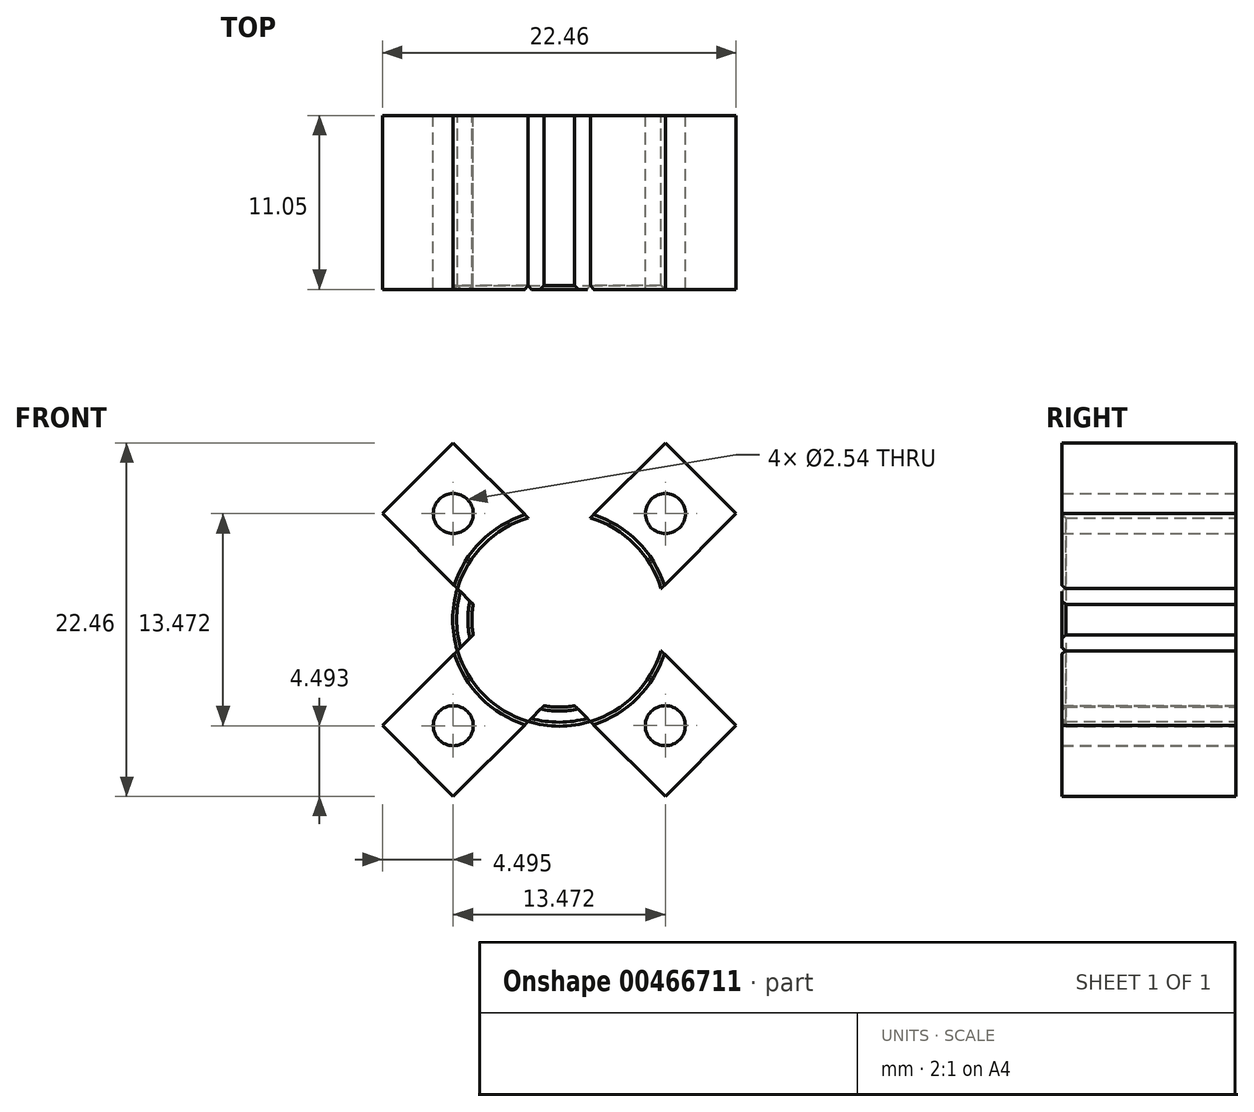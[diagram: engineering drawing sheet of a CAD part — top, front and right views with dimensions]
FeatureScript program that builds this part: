
annotation { "Feature Type Name" : "Feature", "Feature Type Description" : "" }
export const myFeature = defineFeature(function(context is Context, id is Id, definition is map)
    precondition{}
    {
        {
            var Q0;
            Q0=qCreatedBy(makeId("Front.planeOp"),FACE);
            var sketch = newSketch(context, id + "F0", { "sketchPlane" : qUnion([Q0])});
            skLineSegment(sketch, "E0.bottom", {"start": v(11.23, -6.74) * mm, "end": v(-6.74, 11.23) * mm});
            skLineSegment(sketch, "E0.top", {"start": v(6.74, -11.23) * mm, "end": v(-11.23, 6.74) * mm});
            skLineSegment(sketch, "E0.left", {"start": v(11.23, -6.74) * mm, "end": v(6.74, -11.23) * mm});
            skLineSegment(sketch, "E0.right", {"start": v(-6.74, 11.23) * mm, "end": v(-11.23, 6.74) * mm});
            skPoint(sketch, "E0.middle", {"position": v(0, 0) * mm});
            skLineSegment(sketch, "E1.bottom", {"start": v(11.23, 6.73) * mm, "end": v(6.73, 11.23) * mm});
            skLineSegment(sketch, "E1.top", {"start": v(-6.73, -11.23) * mm, "end": v(-11.23, -6.73) * mm});
            skLineSegment(sketch, "E1.left", {"start": v(11.23, 6.73) * mm, "end": v(-6.73, -11.23) * mm});
            skLineSegment(sketch, "E1.right", {"start": v(6.73, 11.23) * mm, "end": v(-11.23, -6.73) * mm});
            skCircle(sketch, "E2", {"center": v(6.74, -6.74) * mm, "radius": 1.27 * mm});
            skCircle(sketch, "E3", {"center": v(-6.73, -6.74) * mm, "radius": 1.27 * mm});
            skCircle(sketch, "E4", {"center": v(-6.74, 6.74) * mm, "radius": 1.27 * mm});
            skCircle(sketch, "E5", {"center": v(6.74, 6.73) * mm, "radius": 1.27 * mm});
            skCircle(sketch, "E6", {"center": v(0, 0) * mm, "radius": 5.56 * mm});
            skCircle(sketch, "E7.0", {"center": v(0, 0) * mm, "radius": 6.77 * mm});
            skSolve(sketch);
        }
        {
            var Q0;
            {var subQ1=sQuery(id+"F0.wireOp",EDGE,"E1.top");Q0=makeQuery(id+"F0.imprint","IMPRINT",FACE,{"disambiguationData":[TD([[makeQuery(id+"F0.imprint","IMPRINT",EDGE,{"derivedFrom":subQ1}),-1.0]])]});}
            var Q1;
            {var subQ0=sQuery(id+"F0.wireOp",EDGE,"E0.left");Q1=makeQuery(id+"F0.imprint","IMPRINT",FACE,{"disambiguationData":[TD([[makeQuery(id+"F0.imprint","IMPRINT",EDGE,{"derivedFrom":subQ0}),-1.0]])]});}
            var Q2;
            {var subQ0=sQuery(id+"F0.wireOp",EDGE,"E0.right");Q2=makeQuery(id+"F0.imprint","IMPRINT",FACE,{"disambiguationData":[TD([[makeQuery(id+"F0.imprint","IMPRINT",EDGE,{"derivedFrom":subQ0}),1.0]])]});}
            var Q3;
            {var subQ1=sQuery(id+"F0.wireOp",EDGE,"E1.bottom");Q3=makeQuery(id+"F0.imprint","IMPRINT",FACE,{"disambiguationData":[TD([[makeQuery(id+"F0.imprint","IMPRINT",EDGE,{"derivedFrom":subQ1}),1.0]])]});}
            var Q4;
            {var subQ0=sQuery(id+"F0.wireOp",EDGE,"E7.0");var subQ1=sQuery(id+"F0.wireOp",EDGE,"E0.top");var subQ2=makeQuery(id+"F0.imprint","INTERSECT",VERTEX,{"disambiguationData":[OD(0.0)],"derivedFrom":[subQ1,subQ0]});Q4=makeQuery(id+"F0.imprint","IMPRINT",FACE,{"disambiguationData":[TD([[makeQuery(id+"F0.imprint","IMPRINT",EDGE,{"disambiguationData":[TD([[subQ2,-1.0]])],"derivedFrom":subQ1}),1.0]])]});}
            var Q5;
            {var subQ0=sQuery(id+"F0.wireOp",EDGE,"E7.0");var subQ1=sQuery(id+"F0.wireOp",EDGE,"E0.bottom");var subQ2=makeQuery(id+"F0.imprint","INTERSECT",VERTEX,{"disambiguationData":[OD(0.0)],"derivedFrom":[subQ1,subQ0]});Q5=makeQuery(id+"F0.imprint","IMPRINT",FACE,{"disambiguationData":[TD([[makeQuery(id+"F0.imprint","IMPRINT",EDGE,{"disambiguationData":[TD([[subQ2,-1.0]])],"derivedFrom":subQ1}),1.0]])]});}
            var Q6;
            {var subQ0=sQuery(id+"F0.wireOp",EDGE,"E7.0");var subQ1=sQuery(id+"F0.wireOp",EDGE,"E1.left");var subQ2=makeQuery(id+"F0.imprint","INTERSECT",VERTEX,{"disambiguationData":[OD(1.0)],"derivedFrom":[subQ1,subQ0]});Q6=makeQuery(id+"F0.imprint","IMPRINT",FACE,{"disambiguationData":[TD([[makeQuery(id+"F0.imprint","IMPRINT",EDGE,{"disambiguationData":[TD([[subQ2,1.0]])],"derivedFrom":subQ1}),-1.0]])]});}
            var Q7;
            {var subQ0=sQuery(id+"F0.wireOp",EDGE,"E7.0");var subQ1=sQuery(id+"F0.wireOp",EDGE,"E0.bottom");var subQ2=makeQuery(id+"F0.imprint","INTERSECT",VERTEX,{"disambiguationData":[OD(0.0)],"derivedFrom":[subQ1,subQ0]});Q7=makeQuery(id+"F0.imprint","IMPRINT",FACE,{"disambiguationData":[TD([[makeQuery(id+"F0.imprint","IMPRINT",EDGE,{"disambiguationData":[TD([[subQ2,-1.0]])],"derivedFrom":subQ1}),-1.0]])]});}
            var Q8;
            {var subQ0=sQuery(id+"F0.wireOp",EDGE,"E7.0");var subQ1=sQuery(id+"F0.wireOp",EDGE,"E1.left");var subQ2=makeQuery(id+"F0.imprint","INTERSECT",VERTEX,{"disambiguationData":[OD(0.0)],"derivedFrom":[subQ1,subQ0]});Q8=makeQuery(id+"F0.imprint","IMPRINT",FACE,{"disambiguationData":[TD([[makeQuery(id+"F0.imprint","IMPRINT",EDGE,{"disambiguationData":[TD([[subQ2,-1.0]])],"derivedFrom":subQ1}),-1.0]])]});}
            var Q9;
            {var subQ0=sQuery(id+"F0.wireOp",EDGE,"E7.0");var subQ1=sQuery(id+"F0.wireOp",EDGE,"E0.bottom");var subQ2=makeQuery(id+"F0.imprint","INTERSECT",VERTEX,{"disambiguationData":[OD(1.0)],"derivedFrom":[subQ1,subQ0]});Q9=makeQuery(id+"F0.imprint","IMPRINT",FACE,{"disambiguationData":[TD([[makeQuery(id+"F0.imprint","IMPRINT",EDGE,{"disambiguationData":[TD([[subQ2,1.0]])],"derivedFrom":subQ1}),-1.0]])]});}
            var Q10;
            {var subQ0=sQuery(id+"F0.wireOp",EDGE,"E7.0");var subQ1=sQuery(id+"F0.wireOp",EDGE,"E0.top");var subQ2=makeQuery(id+"F0.imprint","INTERSECT",VERTEX,{"disambiguationData":[OD(1.0)],"derivedFrom":[subQ1,subQ0]});Q10=makeQuery(id+"F0.imprint","IMPRINT",FACE,{"disambiguationData":[TD([[makeQuery(id+"F0.imprint","IMPRINT",EDGE,{"disambiguationData":[TD([[subQ2,1.0]])],"derivedFrom":subQ1}),1.0]])]});}
            var Q11;
            {var subQ0=sQuery(id+"F0.wireOp",EDGE,"E7.0");var subQ1=sQuery(id+"F0.wireOp",EDGE,"E0.bottom");var subQ2=makeQuery(id+"F0.imprint","INTERSECT",VERTEX,{"disambiguationData":[OD(1.0)],"derivedFrom":[subQ1,subQ0]});Q11=makeQuery(id+"F0.imprint","IMPRINT",FACE,{"disambiguationData":[TD([[makeQuery(id+"F0.imprint","IMPRINT",EDGE,{"disambiguationData":[TD([[subQ2,1.0]])],"derivedFrom":subQ1}),1.0]])]});}
            extrude(context, id + "F1", {"entities" : qUnion([Q0, Q1, Q2, Q3, Q4, Q5, Q6, Q7, Q8, Q9, Q10, Q11]), "depth" : 1.59 * mm});
        }
        {
            var Q0;
            {var subQ0=sQuery(id+"F0.wireOp",EDGE,"E7.0");var subQ1=sQuery(id+"F0.wireOp",EDGE,"E1.left");var subQ2=makeQuery(id+"F0.imprint","INTERSECT",VERTEX,{"disambiguationData":[OD(0.0)],"derivedFrom":[subQ1,subQ0]});Q0=makeQuery(id+"F0.imprint","IMPRINT",FACE,{"disambiguationData":[TD([[makeQuery(id+"F0.imprint","IMPRINT",EDGE,{"disambiguationData":[TD([[subQ2,-1.0]])],"derivedFrom":subQ1}),-1.0]])]});}
            var Q1;
            {var subQ0=sQuery(id+"F0.wireOp",EDGE,"E7.0");var subQ1=sQuery(id+"F0.wireOp",EDGE,"E0.bottom");var subQ2=makeQuery(id+"F0.imprint","INTERSECT",VERTEX,{"disambiguationData":[OD(0.0)],"derivedFrom":[subQ1,subQ0]});Q1=makeQuery(id+"F0.imprint","IMPRINT",FACE,{"disambiguationData":[TD([[makeQuery(id+"F0.imprint","IMPRINT",EDGE,{"disambiguationData":[TD([[subQ2,-1.0]])],"derivedFrom":subQ1}),-1.0]])]});}
            var Q2;
            {var subQ0=sQuery(id+"F0.wireOp",EDGE,"E7.0");var subQ1=sQuery(id+"F0.wireOp",EDGE,"E0.bottom");var subQ2=makeQuery(id+"F0.imprint","INTERSECT",VERTEX,{"disambiguationData":[OD(0.0)],"derivedFrom":[subQ1,subQ0]});Q2=makeQuery(id+"F0.imprint","IMPRINT",FACE,{"disambiguationData":[TD([[makeQuery(id+"F0.imprint","IMPRINT",EDGE,{"disambiguationData":[TD([[subQ2,-1.0]])],"derivedFrom":subQ1}),1.0]])]});}
            var Q3;
            {var subQ0=sQuery(id+"F0.wireOp",EDGE,"E7.0");var subQ1=sQuery(id+"F0.wireOp",EDGE,"E0.top");var subQ2=makeQuery(id+"F0.imprint","INTERSECT",VERTEX,{"disambiguationData":[OD(0.0)],"derivedFrom":[subQ1,subQ0]});Q3=makeQuery(id+"F0.imprint","IMPRINT",FACE,{"disambiguationData":[TD([[makeQuery(id+"F0.imprint","IMPRINT",EDGE,{"disambiguationData":[TD([[subQ2,-1.0]])],"derivedFrom":subQ1}),1.0]])]});}
            var Q4;
            {var subQ0=sQuery(id+"F0.wireOp",EDGE,"E7.0");var subQ1=sQuery(id+"F0.wireOp",EDGE,"E1.left");var subQ2=makeQuery(id+"F0.imprint","INTERSECT",VERTEX,{"disambiguationData":[OD(1.0)],"derivedFrom":[subQ1,subQ0]});Q4=makeQuery(id+"F0.imprint","IMPRINT",FACE,{"disambiguationData":[TD([[makeQuery(id+"F0.imprint","IMPRINT",EDGE,{"disambiguationData":[TD([[subQ2,1.0]])],"derivedFrom":subQ1}),-1.0]])]});}
            var Q5;
            {var subQ0=sQuery(id+"F0.wireOp",EDGE,"E7.0");var subQ1=sQuery(id+"F0.wireOp",EDGE,"E0.top");var subQ2=makeQuery(id+"F0.imprint","INTERSECT",VERTEX,{"disambiguationData":[OD(1.0)],"derivedFrom":[subQ1,subQ0]});Q5=makeQuery(id+"F0.imprint","IMPRINT",FACE,{"disambiguationData":[TD([[makeQuery(id+"F0.imprint","IMPRINT",EDGE,{"disambiguationData":[TD([[subQ2,1.0]])],"derivedFrom":subQ1}),1.0]])]});}
            var Q6;
            {var subQ0=sQuery(id+"F0.wireOp",EDGE,"E7.0");var subQ1=sQuery(id+"F0.wireOp",EDGE,"E0.bottom");var subQ2=makeQuery(id+"F0.imprint","INTERSECT",VERTEX,{"disambiguationData":[OD(1.0)],"derivedFrom":[subQ1,subQ0]});Q6=makeQuery(id+"F0.imprint","IMPRINT",FACE,{"disambiguationData":[TD([[makeQuery(id+"F0.imprint","IMPRINT",EDGE,{"disambiguationData":[TD([[subQ2,1.0]])],"derivedFrom":subQ1}),1.0]])]});}
            var Q7;
            {var subQ0=sQuery(id+"F0.wireOp",EDGE,"E7.0");var subQ1=sQuery(id+"F0.wireOp",EDGE,"E0.bottom");var subQ2=makeQuery(id+"F0.imprint","INTERSECT",VERTEX,{"disambiguationData":[OD(1.0)],"derivedFrom":[subQ1,subQ0]});Q7=makeQuery(id+"F0.imprint","IMPRINT",FACE,{"disambiguationData":[TD([[makeQuery(id+"F0.imprint","IMPRINT",EDGE,{"disambiguationData":[TD([[subQ2,1.0]])],"derivedFrom":subQ1}),-1.0]])]});}
            extrude(context, id + "F2", {"entities" : qUnion([Q0, Q1, Q2, Q3, Q4, Q5, Q6, Q7]), "operationType" : NewBodyOperationType.ADD, "depth" : 11.05 * mm});
        }
        {
            var Q0;
            Q0=makeQuery(id+"F2.opExtrude","CAP_EDGE",EDGE,{"disambiguationData":[OSD([sQuery(id+"F0.wireOp",EDGE,"E7.0")])],"isStart":false});
            var Q1;
            Q1=makeQuery(id+"F2.opExtrude","CAP_EDGE",EDGE,{"disambiguationData":[OSD([sQuery(id+"F0.wireOp",EDGE,"E6")])],"isStart":false});
            chamfer(context, id + "F3", {"entities" : qUnion([Q0, Q1]), "width" : 0.25 * mm});
        }
    });
